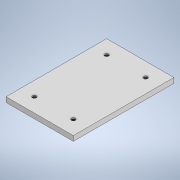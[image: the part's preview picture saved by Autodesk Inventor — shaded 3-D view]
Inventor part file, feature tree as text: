
AUTODESK INVENTOR PART (.ipt)
format: ipt  version: 2020 (Build 240168000, 168)  size: 123,904 bytes
history: native  units: in
note: dims shown in document units (in); Inventor stores cm internally (conversion verified against a paired STEP export)
features: sketch x2, extrude x1, hole x1
ambient origin geometry x8: Origin, YZ Plane, XZ Plane, XY Plane, X Axis, Y Axis, Z Axis, Center Point
bodies: Solid1 (feature_tree)
feature tree (4):
  extrude  "Extrusion1"  Depth=5.0299in
  hole  "Hole1"  [1 undecoded]
  sketch  "Sketch1"  dims[d0=3.3654in d1=5.0299in]
  sketch  "Sketch2"  dims[d2=1.0in d3=135.0deg d4=1.0in d5=1.0in d6=135.0deg d7=1.0in d8=45.0deg d9=0.25in d10=0.0in d11=1.0in d12=135.0deg d13=1.0in d14=135.0deg d15=1.0in d16=45.0deg d17=1.0in d18=45.0deg d19=0.201in d20=0.75in d21=0.375in d22=0.19in d23=0.5635in d24=0.0625in d25=0.8108in]
note: 1 required parameter value undecoded (feature->parameter linkage not recoverable at this tier; creation-order binding heuristic only, values carry confidence <= 0.55)
